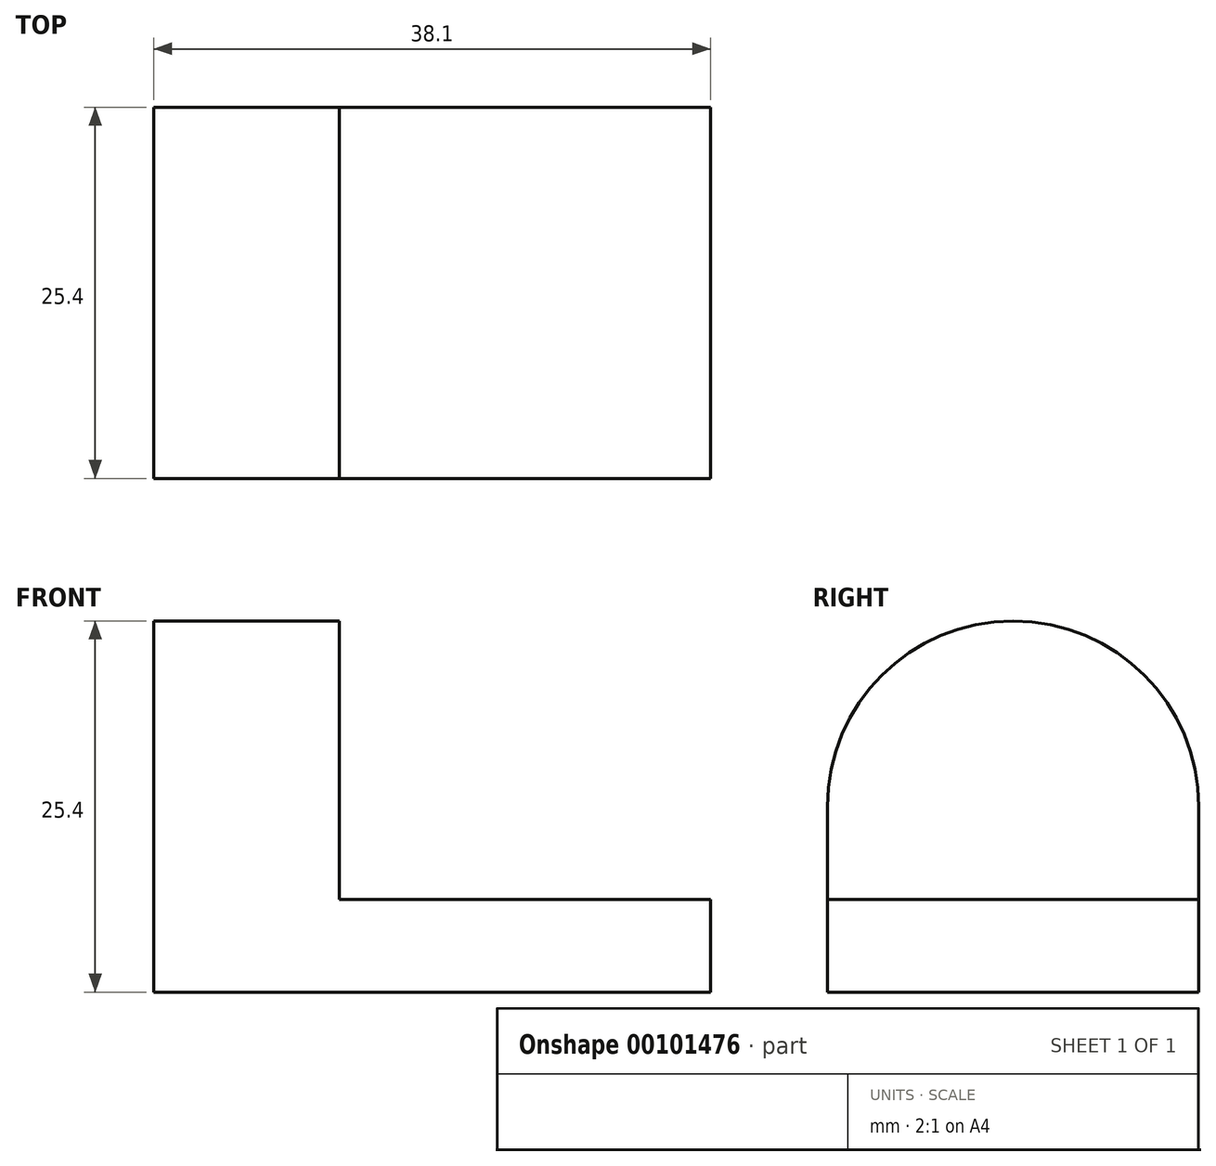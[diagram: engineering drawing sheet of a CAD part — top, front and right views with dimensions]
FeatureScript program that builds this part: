
annotation { "Feature Type Name" : "Feature", "Feature Type Description" : "" }
export const myFeature = defineFeature(function(context is Context, id is Id, definition is map)
    precondition{}
    {
        {
            var Q0;
            Q0=qCreatedBy(makeId("Front.planeOp"),FACE);
            var sketch = newSketch(context, id + "F0", { "sketchPlane" : qUnion([Q0])});
            skLineSegment(sketch, "E0", {"start": v(0, 0) * mm, "end": v(38.1, 0) * mm});
            skLineSegment(sketch, "E1", {"start": v(38.1, 0) * mm, "end": v(38.1, 6.35) * mm});
            skLineSegment(sketch, "E2", {"start": v(38.1, 6.35) * mm, "end": v(0, 6.35) * mm});
            skLineSegment(sketch, "E3", {"start": v(0, 6.35) * mm, "end": v(0, 0) * mm});
            skSolve(sketch);
        }
        {
            var Q0;
            Q0=makeQuery(id+"F0.imprint","IMPRINT",FACE,{"disambiguationData":[TD([[makeQuery(id+"F0.imprint","IMPRINT",EDGE,{"derivedFrom":sQuery(id+"F0.wireOp",EDGE,"E0")}),1.0]])]});
            extrude(context, id + "F1", {"entities" : qUnion([Q0]), "depth" : 25.4 * mm});
        }
        {
            var Q0;
            Q0=qCreatedBy(makeId("Right.planeOp"),FACE);
            var sketch = newSketch(context, id + "F2", { "sketchPlane" : qUnion([Q0])});
            skLineSegment(sketch, "E4", {"start": v(0, 0) * mm, "end": v(-25.4, 0) * mm});
            skLineSegment(sketch, "E5", {"start": v(-25.4, 0) * mm, "end": v(-25.4, 12.7) * mm});
            skLineSegment(sketch, "E6", {"start": v(0, 0) * mm, "end": v(0, 12.7) * mm});
            skArc(sketch, "E7", {"start": v(0, 12.7) * mm, "mid": v(-12.7, 25.4) * mm, "end": v(-25.4, 12.7) * mm});
            skSolve(sketch);
        }
        {
            var Q0;
            Q0=makeQuery(id+"F2.imprint","IMPRINT",FACE,{"disambiguationData":[TD([[makeQuery(id+"F2.imprint","IMPRINT",EDGE,{"derivedFrom":sQuery(id+"F2.wireOp",EDGE,"E4")}),-1.0]])]});
            extrude(context, id + "F3", {"entities" : qUnion([Q0]), "operationType" : NewBodyOperationType.ADD, "depth" : 12.7 * mm});
        }
    });
